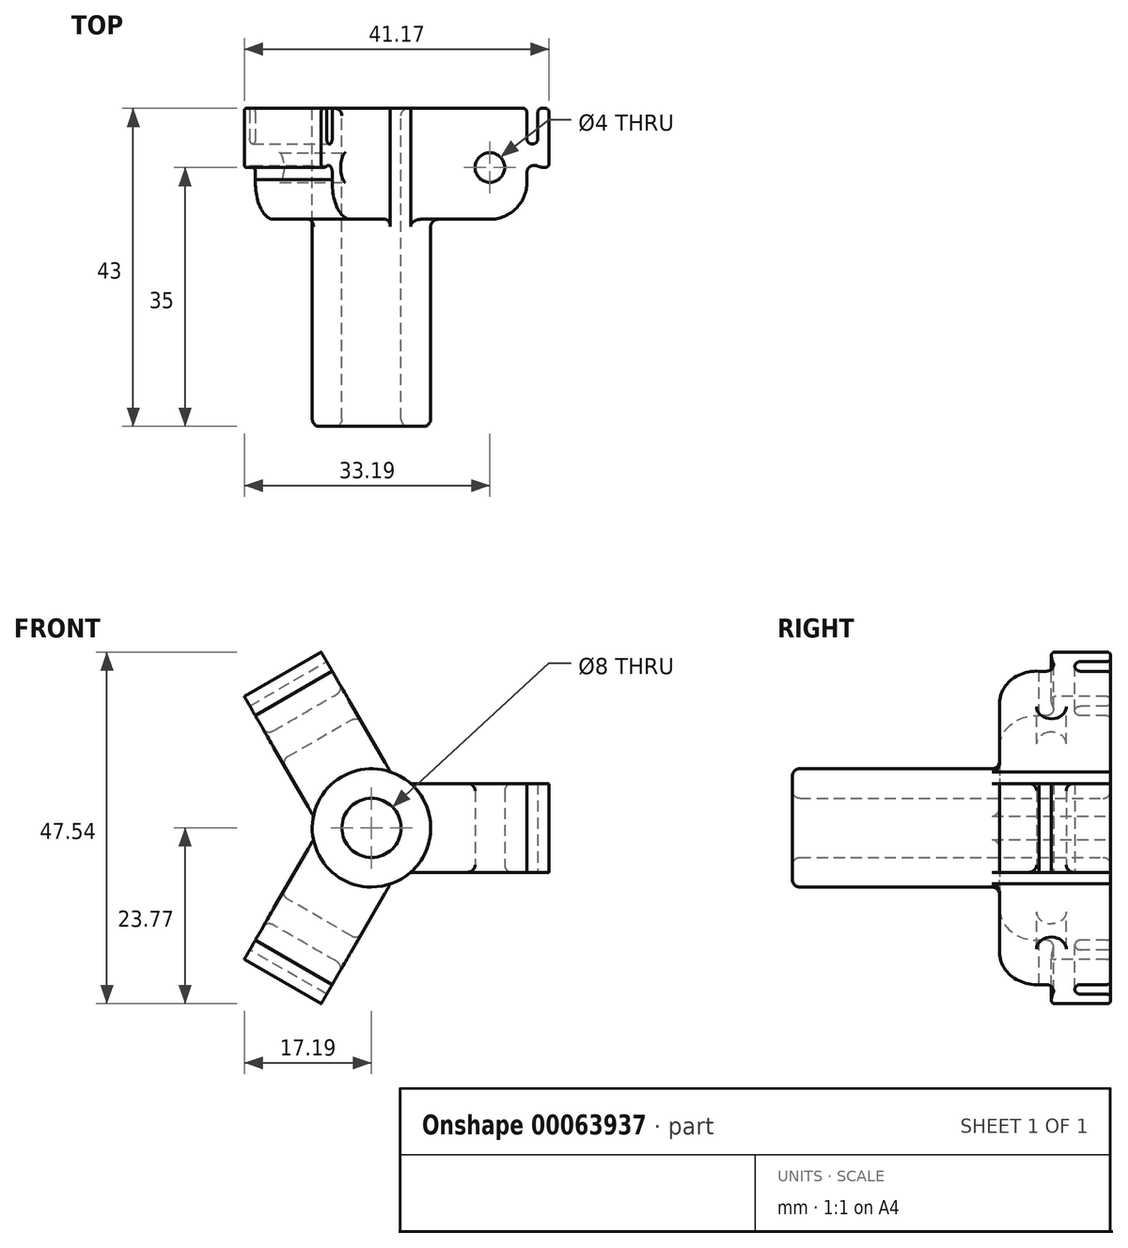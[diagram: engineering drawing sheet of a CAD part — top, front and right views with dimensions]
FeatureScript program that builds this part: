
annotation { "Feature Type Name" : "Feature", "Feature Type Description" : "" }
export const myFeature = defineFeature(function(context is Context, id is Id, definition is map)
    precondition{}
    {
        {
            var Q0;
            Q0=qCreatedBy(makeId("Front.planeOp"),FACE);
            var sketch = newSketch(context, id + "F0", { "sketchPlane" : qUnion([Q0])});
            skCircle(sketch, "E0.0", {"center": v(-66, 0) * mm, "radius": 4 * mm});
            skCircle(sketch, "E1", {"center": v(-66, 0) * mm, "radius": 8 * mm});
            skLineSegment(sketch, "E2", {"start": v(-56, -1.5) * mm, "end": v(-56, 1.5) * mm, "construction": true});
            skSolve(sketch);
        }
        {
            var Q0;
            Q0=qSketchRegion(id+"F0",true);
            extrude(context, id + "F1", {"entities" : qUnion([Q0]), "depth" : 35 * mm, "hasSecondDirection" : true, "secondDirectionOppositeDirection" : true, "secondDirectionDepth" : 8 * mm});
        }
        {
            var Q0;
            Q0=qCreatedBy(makeId("Top.planeOp"),FACE);
            var sketch = newSketch(context, id + "F2", { "sketchPlane" : qUnion([Q0])});
            skLineSegment(sketch, "E3.filletArc", {"start": v(-50, 3) * mm, "end": v(-50, 3) * mm});
            skCircle(sketch, "E4.0", {"center": v(-50, 0) * mm, "radius": 2 * mm});
            skLineSegment(sketch, "E5.0", {"start": v(-62, 8) * mm, "end": v(-70, 8) * mm, "construction": true});
            skLineSegment(sketch, "E6", {"start": v(-62, 8) * mm, "end": v(-62, -27.53) * mm});
            skLineSegment(sketch, "E7", {"start": v(-50, -7) * mm, "end": v(-62, -7) * mm});
            skLineSegment(sketch, "E8", {"start": v(-50, 3) * mm, "end": v(-50, -7) * mm, "construction": true});
            skArc(sketch, "E9.0", {"start": v(-45.84, -4.78) * mm, "mid": v(-55, -2) * mm, "end": v(-45.84, 0.78) * mm, "construction": true});
            skArc(sketch, "E10", {"start": v(-50, -7) * mm, "mid": v(-46.35, -5.42) * mm, "end": v(-45.01, -1.67) * mm});
            skLineSegment(sketch, "E11", {"start": v(-45.5, 8) * mm, "end": v(-62, 8) * mm});
            skArc(sketch, "E12", {"start": v(-45, 7.5) * mm, "mid": v(-45.15, 7.85) * mm, "end": v(-45.5, 8) * mm});
            skLineSegment(sketch, "E13", {"start": v(-45, 7.5) * mm, "end": v(-45, 3.92) * mm});
            skArc(sketch, "E14", {"start": v(-45, 3.92) * mm, "mid": v(-44.26, 3.17) * mm, "end": v(-43.5, 3.92) * mm});
            skArc(sketch, "E15", {"start": v(-42.02, 7.5) * mm, "mid": v(-42.16, 7.85) * mm, "end": v(-42.52, 8) * mm});
            skLineSegment(sketch, "E16", {"start": v(-42.52, 8) * mm, "end": v(-43, 8) * mm});
            skArc(sketch, "E17", {"start": v(-43, 8) * mm, "mid": v(-43.36, 7.85) * mm, "end": v(-43.5, 7.5) * mm});
            skLineSegment(sketch, "E18", {"start": v(-43.5, 7.5) * mm, "end": v(-43.5, 3.92) * mm});
            skArc(sketch, "E19.0", {"start": v(-45.01, 1.33) * mm, "mid": v(-43.93, 0.35) * mm, "end": v(-42.52, 0) * mm});
            skLineSegment(sketch, "E20", {"start": v(-42.02, 7.5) * mm, "end": v(-42.02, 0.5) * mm});
            skArc(sketch, "E21", {"start": v(-42.52, 0) * mm, "mid": v(-42.16, 0.15) * mm, "end": v(-42.02, 0.5) * mm});
            skLineSegment(sketch, "E22", {"start": v(-45.01, 1.33) * mm, "end": v(-45.01, -1.67) * mm});
            skSolve(sketch);
        }
        {
            var Q0;
            Q0=qSketchRegion(id+"F2",true);
            extrude(context, id + "F3", {"entities" : qUnion([Q0]), "endBound" : BoundingType.SYMMETRIC, "depth" : 12 * mm, "hasSecondDirection" : true, "secondDirectionOppositeDirection" : false, "secondDirectionDepth" : 0.5 * mm});
        }
        {
            var Q0;
            Q0=makeQuery(id+"F3.opExtrude","CAP_EDGE",EDGE,{"disambiguationData":[OSD([sQuery(id+"F2.wireOp",EDGE,"bcf398e5-bbe5-4ac5-b800-1ac8445f6ca1.bottom")])],"isStart":false});
            var Q1;
            Q1=makeQuery(id+"F3.opExtrude","CAP_EDGE",EDGE,{"disambiguationData":[OSD([sQuery(id+"F2.wireOp",EDGE,"E4.0")])],"isStart":false});
            var Q2;
            Q2=makeQuery(id+"F3.opExtrude","CAP_EDGE",EDGE,{"disambiguationData":[OSD([sQuery(id+"F2.wireOp",EDGE,"69baed6d-7b14-42b7-8c43-25618c10141b")])],"isStart":true});
            var Q3;
            Q3=makeQuery(id+"F3.opExtrude","CAP_EDGE",EDGE,{"disambiguationData":[OSD([sQuery(id+"F2.wireOp",EDGE,"E4.0")])],"isStart":true});
            var Q4;
            Q4=makeQuery(id+"F3.opExtrude","CAP_EDGE",EDGE,{"disambiguationData":[OSD([sQuery(id+"F2.wireOp",EDGE,"e079cdc6-f3e3-49d5-83fb-a535cef789e9")])],"isStart":true});
            var Q5;
            Q5=makeQuery(id+"F3.opExtrude","CAP_EDGE",EDGE,{"disambiguationData":[OSD([sQuery(id+"F2.wireOp",EDGE,"27f87ce1-439b-4c83-b674-5cf24daf7377")])],"isStart":true});
            var Q6;
            Q6=makeQuery(id+"F3.opExtrude","CAP_EDGE",EDGE,{"disambiguationData":[OSD([sQuery(id+"F2.wireOp",EDGE,"E6")])],"isStart":false});
            fillet(context, id + "F4", {"entities" : qUnion([Q0, Q1, Q2, Q3, Q4, Q5, Q6]), "radius" : 1 * mm, "tangentPropagation" : true, "allowEdgeOverflow" : false});
        }
        {
            var Q0;
            Q0=makeQuery(id+"F3.opExtrude","SWEPT_BODY",BODY,{"disambiguationData":[OSD([sQuery(id+"F2.wireOp",EDGE,"bcf398e5-bbe5-4ac5-b800-1ac8445f6ca1.bottom"),sQuery(id+"F2.wireOp",EDGE,"bcf398e5-bbe5-4ac5-b800-1ac8445f6ca1.left"),sQuery(id+"F2.wireOp",EDGE,"bcf398e5-bbe5-4ac5-b800-1ac8445f6ca1.right"),sQuery(id+"F2.wireOp",EDGE,"E3.filletArc"),sQuery(id+"F2.wireOp",EDGE,"7d993716-79a0-4fe6-a2a7-4d4d2bbec964"),sQuery(id+"F2.wireOp",EDGE,"3825c2cf-9032-4a16-8e50-70d36997c3e9"),sQuery(id+"F2.wireOp",EDGE,"E4.0"),sQuery(id+"F2.wireOp",EDGE,"69baed6d-7b14-42b7-8c43-25618c10141b")])]});
            var Q1;
            Q1=makeQuery(id+"F1.opExtrude","CAP_EDGE",EDGE,{"disambiguationData":[OSD([sQuery(id+"F0.wireOp",EDGE,"E0.0")])],"isStart":false});
            circularPattern(context, id + "F5", {"operationType" : NewBodyOperationType.ADD, "entities" : qUnion([Q0]), "axis" : qUnion([Q1]), "angle" : 360 * degree, "instanceCount" : round(3), "equalSpace" : true});
        }
        {
            var Q0;
            Q0=makeQuery(id+"F1.opExtrude","CAP_FACE",FACE,{"disambiguationData":[OSD([sQuery(id+"F0.wireOp",EDGE,"E0.0"),sQuery(id+"F0.wireOp",EDGE,"E1")])],"isStart":false});
            var Q1;
            Q1=makeQuery(id+"F5.boolean.opBoolean","INTERSECT",EDGE,{"derivedFrom":[makeQuery(id+"F1.opExtrude","SWEPT_FACE",FACE,{"disambiguationData":[OSD([sQuery(id+"F0.wireOp",EDGE,"E1")])]}),makeQuery(id+"F3.opExtrude","SWEPT_FACE",FACE,{"disambiguationData":[OSD([sQuery(id+"F2.wireOp",EDGE,"E7")])]})]});
            var Q2;
            Q2=makeQuery(id+"F5.boolean.opBoolean","INTERSECT",EDGE,{"derivedFrom":[makeQuery(id+"F1.opExtrude","SWEPT_FACE",FACE,{"disambiguationData":[OSD([sQuery(id+"F0.wireOp",EDGE,"E1")])]}),makeQuery(id+"F5.opPattern","COPY",FACE,{"derivedFrom":makeQuery(id+"FA9idb4laBfHRd9_3.opPattern","COPY",FACE,{"derivedFrom":makeQuery(id+"F3.opExtrude","SWEPT_FACE",FACE,{"disambiguationData":[OSD([sQuery(id+"F2.wireOp",EDGE,"E7")])]}),"instanceName":"1"}),"instanceName":"1"})]});
            var Q3;
            Q3=makeQuery(id+"F5.boolean.opBoolean","INTERSECT",EDGE,{"derivedFrom":[makeQuery(id+"F1.opExtrude","SWEPT_FACE",FACE,{"disambiguationData":[OSD([sQuery(id+"F0.wireOp",EDGE,"E1")])]}),makeQuery(id+"F5.opPattern","COPY",FACE,{"derivedFrom":makeQuery(id+"F3.opExtrude","SWEPT_FACE",FACE,{"disambiguationData":[OSD([sQuery(id+"F2.wireOp",EDGE,"E7")])]}),"instanceName":"1"})]});
            var Q4;
            Q4=makeQuery(id+"F5.boolean.opBoolean","INTERSECT",EDGE,{"derivedFrom":[makeQuery(id+"F1.opExtrude","SWEPT_FACE",FACE,{"disambiguationData":[OSD([sQuery(id+"F0.wireOp",EDGE,"E1")])]}),makeQuery(id+"FA9idb4laBfHRd9_3.opPattern","COPY",FACE,{"derivedFrom":makeQuery(id+"F3.opExtrude","SWEPT_FACE",FACE,{"disambiguationData":[OSD([sQuery(id+"F2.wireOp",EDGE,"E7")])]}),"instanceName":"1"})]});
            var Q5;
            Q5=makeQuery(id+"F5.boolean.opBoolean","INTERSECT",EDGE,{"derivedFrom":[makeQuery(id+"F1.opExtrude","SWEPT_FACE",FACE,{"disambiguationData":[OSD([sQuery(id+"F0.wireOp",EDGE,"E1")])]}),makeQuery(id+"F5.opPattern","COPY",FACE,{"derivedFrom":makeQuery(id+"F3.opExtrude","SWEPT_FACE",FACE,{"disambiguationData":[OSD([sQuery(id+"F2.wireOp",EDGE,"E7")])]}),"instanceName":"2"})]});
            var Q6;
            Q6=makeQuery(id+"F5.boolean.opBoolean","INTERSECT",EDGE,{"derivedFrom":[makeQuery(id+"F1.opExtrude","SWEPT_FACE",FACE,{"disambiguationData":[OSD([sQuery(id+"F0.wireOp",EDGE,"E1")])]}),makeQuery(id+"F5.opPattern","COPY",FACE,{"derivedFrom":makeQuery(id+"FA9idb4laBfHRd9_3.opPattern","COPY",FACE,{"derivedFrom":makeQuery(id+"F3.opExtrude","SWEPT_FACE",FACE,{"disambiguationData":[OSD([sQuery(id+"F2.wireOp",EDGE,"E7")])]}),"instanceName":"1"}),"instanceName":"2"})]});
            var Q7;
            {var subQ0=sQuery(id+"F0.wireOp",EDGE,"E1");var subQ1=sQuery(id+"F2.wireOp",EDGE,"bcf398e5-bbe5-4ac5-b800-1ac8445f6ca1.bottom");Q7=makeQuery(id+"F5.boolean.opBoolean","SPLIT",EDGE,{"disambiguationData":[TD([makeQuery(id+"F5.opPattern","COPY",FACE,{"derivedFrom":makeQuery(id+"F4.opFillet","BLEND_FACE",FACE,{"disambiguationData":[OSD([subQ1]),TDD([makeQuery(id+"F3.opExtrude","CAP_EDGE",EDGE,{"disambiguationData":[OSD([subQ1])],"isStart":true})])]}),"instanceName":"2"})])],"derivedFrom":makeQuery(id+"F1.opExtrude","CAP_EDGE",EDGE,{"disambiguationData":[OSD([subQ0])],"isStart":true})});}
            var Q8;
            {var subQ0=sQuery(id+"F0.wireOp",EDGE,"E1");var subQ1=sQuery(id+"F2.wireOp",EDGE,"bcf398e5-bbe5-4ac5-b800-1ac8445f6ca1.bottom");Q8=makeQuery(id+"F5.boolean.opBoolean","SPLIT",EDGE,{"disambiguationData":[TD([makeQuery(id+"F4.opFillet","BLEND_FACE",FACE,{"disambiguationData":[OSD([subQ1]),TDD([makeQuery(id+"F3.opExtrude","CAP_EDGE",EDGE,{"disambiguationData":[OSD([subQ1])],"isStart":true})])]})])],"derivedFrom":makeQuery(id+"F1.opExtrude","CAP_EDGE",EDGE,{"disambiguationData":[OSD([subQ0])],"isStart":true})});}
            var Q9;
            {var subQ0=sQuery(id+"F0.wireOp",EDGE,"E1");var subQ1=sQuery(id+"F2.wireOp",EDGE,"bcf398e5-bbe5-4ac5-b800-1ac8445f6ca1.bottom");Q9=makeQuery(id+"F5.boolean.opBoolean","SPLIT",EDGE,{"disambiguationData":[TD([makeQuery(id+"F5.opPattern","COPY",FACE,{"derivedFrom":makeQuery(id+"F4.opFillet","BLEND_FACE",FACE,{"disambiguationData":[OSD([subQ1]),TDD([makeQuery(id+"F3.opExtrude","CAP_EDGE",EDGE,{"disambiguationData":[OSD([subQ1])],"isStart":true})])]}),"instanceName":"1"})])],"derivedFrom":makeQuery(id+"F1.opExtrude","CAP_EDGE",EDGE,{"disambiguationData":[OSD([subQ0])],"isStart":true})});}
            var Q10;
            Q10=makeQuery(id+"F1.opExtrude","CAP_EDGE",EDGE,{"disambiguationData":[OSD([sQuery(id+"F0.wireOp",EDGE,"E0.0")])],"isStart":true});
            var Q11;
            {var subQ0=sQuery(id+"F2.wireOp",EDGE,"E19.0");var subQ1=sQuery(id+"F2.wireOp",EDGE,"E22");var subQ2=sQuery(id+"FNeipIwRU9zdJoM_3.wireOp",EDGE,"a3996003-e145-4080-a589-fa3d7a471764");Q11=makeQuery(id+"F5.opPattern","COPY",EDGE,{"derivedFrom":makeQuery(id+"FYFrIHL945fgIyR_3.boolean.opBoolean","SPLIT",EDGE,{"disambiguationData":[TD([makeQuery(id+"FYFrIHL945fgIyR_3.opExtrude","CAP_FACE",FACE,{"disambiguationData":[OSD([sQuery(id+"FNeipIwRU9zdJoM_3.wireOp",EDGE,"fa8f3cbd-8554-450e-a138-bf820a938248.0"),sQuery(id+"FNeipIwRU9zdJoM_3.wireOp",EDGE,"d497bfc0-c988-4c61-9718-408c56727f98"),sQuery(id+"FNeipIwRU9zdJoM_3.wireOp",EDGE,"8ce20f3b-937c-476f-a059-e8f4e0a3011d"),sQuery(id+"FNeipIwRU9zdJoM_3.wireOp",EDGE,"cc079d82-4f95-4c09-8403-123b4630d993.0"),sQuery(id+"FNeipIwRU9zdJoM_3.wireOp",EDGE,"e6e2b761-f98e-43ba-bbe1-079cadf7413c.0"),sQuery(id+"FNeipIwRU9zdJoM_3.wireOp",EDGE,"ab0ec8ac-8a4f-423f-85da-5baed9086eda.0"),subQ2,sQuery(id+"FNeipIwRU9zdJoM_3.wireOp",EDGE,"79814c29-a62d-403a-9d46-4655cf4f59c6")])],"isStart":false})])],"derivedFrom":makeQuery(id+"F3.opExtrude","SWEPT_EDGE",EDGE,{"disambiguationData":[OSD([subQ0,subQ1])]})}),"instanceName":"2"});}
            var Q12;
            {var subQ0=sQuery(id+"F2.wireOp",EDGE,"E19.0");var subQ1=sQuery(id+"F2.wireOp",EDGE,"E22");var subQ2=sQuery(id+"FNeipIwRU9zdJoM_3.wireOp",EDGE,"a3996003-e145-4080-a589-fa3d7a471764");Q12=makeQuery(id+"F5.opPattern","COPY",EDGE,{"derivedFrom":makeQuery(id+"FYFrIHL945fgIyR_3.boolean.opBoolean","SPLIT",EDGE,{"disambiguationData":[TD([makeQuery(id+"FYFrIHL945fgIyR_3.opExtrude","CAP_FACE",FACE,{"disambiguationData":[OSD([sQuery(id+"FNeipIwRU9zdJoM_3.wireOp",EDGE,"fa8f3cbd-8554-450e-a138-bf820a938248.0"),sQuery(id+"FNeipIwRU9zdJoM_3.wireOp",EDGE,"d497bfc0-c988-4c61-9718-408c56727f98"),sQuery(id+"FNeipIwRU9zdJoM_3.wireOp",EDGE,"8ce20f3b-937c-476f-a059-e8f4e0a3011d"),sQuery(id+"FNeipIwRU9zdJoM_3.wireOp",EDGE,"cc079d82-4f95-4c09-8403-123b4630d993.0"),sQuery(id+"FNeipIwRU9zdJoM_3.wireOp",EDGE,"e6e2b761-f98e-43ba-bbe1-079cadf7413c.0"),sQuery(id+"FNeipIwRU9zdJoM_3.wireOp",EDGE,"ab0ec8ac-8a4f-423f-85da-5baed9086eda.0"),subQ2,sQuery(id+"FNeipIwRU9zdJoM_3.wireOp",EDGE,"79814c29-a62d-403a-9d46-4655cf4f59c6")])],"isStart":true})])],"derivedFrom":makeQuery(id+"F3.opExtrude","SWEPT_EDGE",EDGE,{"disambiguationData":[OSD([subQ0,subQ1])]})}),"instanceName":"2"});}
            var Q13;
            {var subQ0=sQuery(id+"F2.wireOp",EDGE,"E19.0");var subQ1=sQuery(id+"F2.wireOp",EDGE,"E22");var subQ2=sQuery(id+"FNeipIwRU9zdJoM_3.wireOp",EDGE,"a3996003-e145-4080-a589-fa3d7a471764");Q13=makeQuery(id+"F5.opPattern","COPY",EDGE,{"derivedFrom":makeQuery(id+"FYFrIHL945fgIyR_3.boolean.opBoolean","SPLIT",EDGE,{"disambiguationData":[TD([makeQuery(id+"FYFrIHL945fgIyR_3.opExtrude","CAP_FACE",FACE,{"disambiguationData":[OSD([sQuery(id+"FNeipIwRU9zdJoM_3.wireOp",EDGE,"fa8f3cbd-8554-450e-a138-bf820a938248.0"),sQuery(id+"FNeipIwRU9zdJoM_3.wireOp",EDGE,"d497bfc0-c988-4c61-9718-408c56727f98"),sQuery(id+"FNeipIwRU9zdJoM_3.wireOp",EDGE,"8ce20f3b-937c-476f-a059-e8f4e0a3011d"),sQuery(id+"FNeipIwRU9zdJoM_3.wireOp",EDGE,"cc079d82-4f95-4c09-8403-123b4630d993.0"),sQuery(id+"FNeipIwRU9zdJoM_3.wireOp",EDGE,"e6e2b761-f98e-43ba-bbe1-079cadf7413c.0"),sQuery(id+"FNeipIwRU9zdJoM_3.wireOp",EDGE,"ab0ec8ac-8a4f-423f-85da-5baed9086eda.0"),subQ2,sQuery(id+"FNeipIwRU9zdJoM_3.wireOp",EDGE,"79814c29-a62d-403a-9d46-4655cf4f59c6")])],"isStart":true})])],"derivedFrom":makeQuery(id+"F3.opExtrude","SWEPT_EDGE",EDGE,{"disambiguationData":[OSD([subQ0,subQ1])]})}),"instanceName":"1"});}
            var Q14;
            {var subQ0=sQuery(id+"F2.wireOp",EDGE,"E19.0");var subQ1=sQuery(id+"F2.wireOp",EDGE,"E22");var subQ2=sQuery(id+"FNeipIwRU9zdJoM_3.wireOp",EDGE,"a3996003-e145-4080-a589-fa3d7a471764");Q14=makeQuery(id+"F5.opPattern","COPY",EDGE,{"derivedFrom":makeQuery(id+"FYFrIHL945fgIyR_3.boolean.opBoolean","SPLIT",EDGE,{"disambiguationData":[TD([makeQuery(id+"FYFrIHL945fgIyR_3.opExtrude","CAP_FACE",FACE,{"disambiguationData":[OSD([sQuery(id+"FNeipIwRU9zdJoM_3.wireOp",EDGE,"fa8f3cbd-8554-450e-a138-bf820a938248.0"),sQuery(id+"FNeipIwRU9zdJoM_3.wireOp",EDGE,"d497bfc0-c988-4c61-9718-408c56727f98"),sQuery(id+"FNeipIwRU9zdJoM_3.wireOp",EDGE,"8ce20f3b-937c-476f-a059-e8f4e0a3011d"),sQuery(id+"FNeipIwRU9zdJoM_3.wireOp",EDGE,"cc079d82-4f95-4c09-8403-123b4630d993.0"),sQuery(id+"FNeipIwRU9zdJoM_3.wireOp",EDGE,"e6e2b761-f98e-43ba-bbe1-079cadf7413c.0"),sQuery(id+"FNeipIwRU9zdJoM_3.wireOp",EDGE,"ab0ec8ac-8a4f-423f-85da-5baed9086eda.0"),subQ2,sQuery(id+"FNeipIwRU9zdJoM_3.wireOp",EDGE,"79814c29-a62d-403a-9d46-4655cf4f59c6")])],"isStart":false})])],"derivedFrom":makeQuery(id+"F3.opExtrude","SWEPT_EDGE",EDGE,{"disambiguationData":[OSD([subQ0,subQ1])]})}),"instanceName":"1"});}
            var Q15;
            {var subQ0=sQuery(id+"F2.wireOp",EDGE,"E19.0");var subQ1=sQuery(id+"F2.wireOp",EDGE,"E22");var subQ2=sQuery(id+"FNeipIwRU9zdJoM_3.wireOp",EDGE,"a3996003-e145-4080-a589-fa3d7a471764");Q15=makeQuery(id+"FYFrIHL945fgIyR_3.boolean.opBoolean","SPLIT",EDGE,{"disambiguationData":[TD([makeQuery(id+"FYFrIHL945fgIyR_3.opExtrude","CAP_FACE",FACE,{"disambiguationData":[OSD([sQuery(id+"FNeipIwRU9zdJoM_3.wireOp",EDGE,"fa8f3cbd-8554-450e-a138-bf820a938248.0"),sQuery(id+"FNeipIwRU9zdJoM_3.wireOp",EDGE,"d497bfc0-c988-4c61-9718-408c56727f98"),sQuery(id+"FNeipIwRU9zdJoM_3.wireOp",EDGE,"8ce20f3b-937c-476f-a059-e8f4e0a3011d"),sQuery(id+"FNeipIwRU9zdJoM_3.wireOp",EDGE,"cc079d82-4f95-4c09-8403-123b4630d993.0"),sQuery(id+"FNeipIwRU9zdJoM_3.wireOp",EDGE,"e6e2b761-f98e-43ba-bbe1-079cadf7413c.0"),sQuery(id+"FNeipIwRU9zdJoM_3.wireOp",EDGE,"ab0ec8ac-8a4f-423f-85da-5baed9086eda.0"),subQ2,sQuery(id+"FNeipIwRU9zdJoM_3.wireOp",EDGE,"79814c29-a62d-403a-9d46-4655cf4f59c6")])],"isStart":true})])],"derivedFrom":makeQuery(id+"F3.opExtrude","SWEPT_EDGE",EDGE,{"disambiguationData":[OSD([subQ0,subQ1])]})});}
            var Q16;
            {var subQ0=sQuery(id+"F2.wireOp",EDGE,"E19.0");var subQ1=sQuery(id+"F2.wireOp",EDGE,"E22");var subQ2=sQuery(id+"FNeipIwRU9zdJoM_3.wireOp",EDGE,"a3996003-e145-4080-a589-fa3d7a471764");Q16=makeQuery(id+"FYFrIHL945fgIyR_3.boolean.opBoolean","SPLIT",EDGE,{"disambiguationData":[TD([makeQuery(id+"FYFrIHL945fgIyR_3.opExtrude","CAP_FACE",FACE,{"disambiguationData":[OSD([sQuery(id+"FNeipIwRU9zdJoM_3.wireOp",EDGE,"fa8f3cbd-8554-450e-a138-bf820a938248.0"),sQuery(id+"FNeipIwRU9zdJoM_3.wireOp",EDGE,"d497bfc0-c988-4c61-9718-408c56727f98"),sQuery(id+"FNeipIwRU9zdJoM_3.wireOp",EDGE,"8ce20f3b-937c-476f-a059-e8f4e0a3011d"),sQuery(id+"FNeipIwRU9zdJoM_3.wireOp",EDGE,"cc079d82-4f95-4c09-8403-123b4630d993.0"),sQuery(id+"FNeipIwRU9zdJoM_3.wireOp",EDGE,"e6e2b761-f98e-43ba-bbe1-079cadf7413c.0"),sQuery(id+"FNeipIwRU9zdJoM_3.wireOp",EDGE,"ab0ec8ac-8a4f-423f-85da-5baed9086eda.0"),subQ2,sQuery(id+"FNeipIwRU9zdJoM_3.wireOp",EDGE,"79814c29-a62d-403a-9d46-4655cf4f59c6")])],"isStart":false})])],"derivedFrom":makeQuery(id+"F3.opExtrude","SWEPT_EDGE",EDGE,{"disambiguationData":[OSD([subQ0,subQ1])]})});}
            fillet(context, id + "F6", {"entities" : qUnion([Q0, Q1, Q2, Q3, Q4, Q5, Q6, Q7, Q8, Q9, Q10, Q11, Q12, Q13, Q14, Q15, Q16]), "radius" : 1 * mm, "tangentPropagation" : true, "allowEdgeOverflow" : false});
        }
    });
